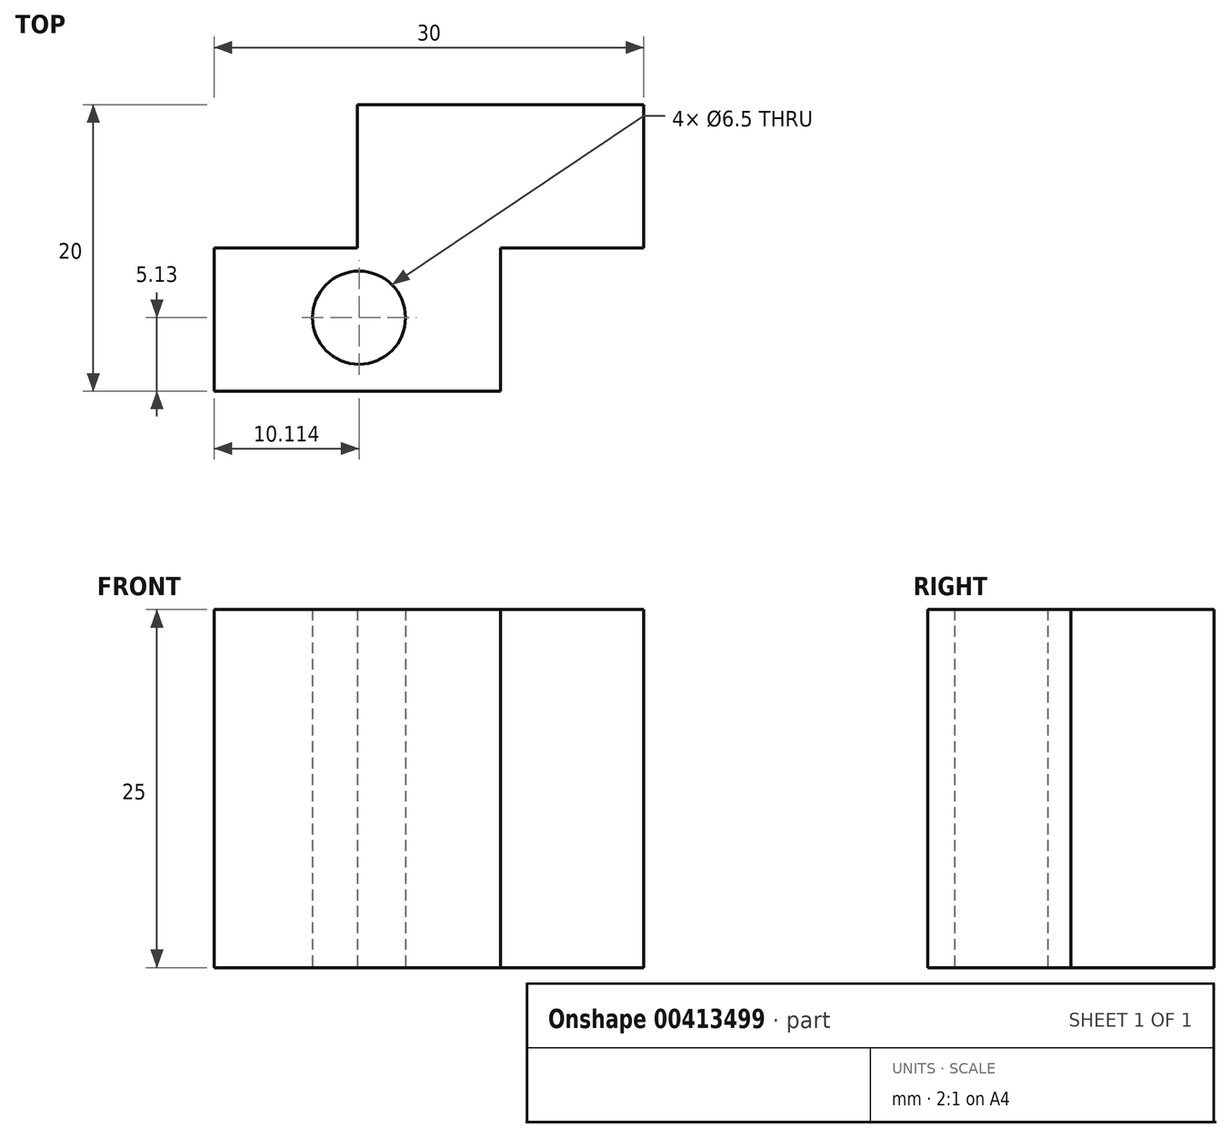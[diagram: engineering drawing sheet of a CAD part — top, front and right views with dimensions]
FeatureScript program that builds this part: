
annotation { "Feature Type Name" : "Feature", "Feature Type Description" : "" }
export const myFeature = defineFeature(function(context is Context, id is Id, definition is map)
    precondition{}
    {
        {
            var Q0;
            Q0=qCreatedBy(makeId("Top.planeOp"),FACE);
            var sketch = newSketch(context, id + "F0", { "sketchPlane" : qUnion([Q0])});
            skLineSegment(sketch, "E0.bottom", {"start": v(-7.6, 20) * mm, "end": v(12.4, 20) * mm});
            skLineSegment(sketch, "E0.top", {"start": v(-7.6, 10) * mm, "end": v(12.4, 10) * mm});
            skLineSegment(sketch, "E0.left", {"start": v(-7.6, 20) * mm, "end": v(-7.6, 10) * mm});
            skLineSegment(sketch, "E0.right", {"start": v(12.4, 20) * mm, "end": v(12.4, 10) * mm});
            skLineSegment(sketch, "E1.bottom", {"start": v(2.4, 10) * mm, "end": v(-17.6, 10) * mm});
            skLineSegment(sketch, "E1.top", {"start": v(2.4, 0) * mm, "end": v(-17.6, 0) * mm});
            skLineSegment(sketch, "E1.left", {"start": v(2.4, 10) * mm, "end": v(2.4, 0) * mm});
            skLineSegment(sketch, "E1.right", {"start": v(-17.6, 10) * mm, "end": v(-17.6, 0) * mm});
            skLineSegment(sketch, "E2.bottom", {"start": v(2.4, 10) * mm, "end": v(22.4, 10) * mm});
            skLineSegment(sketch, "E2.top", {"start": v(2.4, 0) * mm, "end": v(22.4, 0) * mm});
            skLineSegment(sketch, "E2.right", {"start": v(22.4, 10) * mm, "end": v(22.4, 0) * mm});
            skCircle(sketch, "E3", {"center": v(-7.49, 5.13) * mm, "radius": 3.25 * mm});
            skCircle(sketch, "E4", {"center": v(12.34, 4.85) * mm, "radius": 3.25 * mm});
            skPoint(sketch, "E5.end.orphan", {"position": v(12.4, 4.85) * mm});
            skSolve(sketch);
        }
        {
            var Q0;
            Q0=makeQuery(id+"F0.imprint","IMPRINT",FACE,{"disambiguationData":[TD([[makeQuery(id+"F0.imprint","IMPRINT",EDGE,{"derivedFrom":sQuery(id+"F0.wireOp",EDGE,"E0.bottom")}),-1.0]])]});
            var Q1;
            {var subQ4=sQuery(id+"F0.wireOp",EDGE,"E1.left");Q1=makeQuery(id+"F0.imprint","IMPRINT",FACE,{"disambiguationData":[TD([[makeQuery(id+"F0.imprint","IMPRINT",EDGE,{"derivedFrom":subQ4}),1.0]])]});}
            var Q2;
            {var subQ0=sQuery(id+"F0.wireOp",EDGE,"E1.right");Q2=makeQuery(id+"F0.imprint","IMPRINT",FACE,{"disambiguationData":[TD([[makeQuery(id+"F0.imprint","IMPRINT",EDGE,{"derivedFrom":subQ0}),1.0]])]});}
            extrude(context, id + "F1", {"entities" : qUnion([Q0, Q1, Q2]), "depth" : 25 * mm});
        }
    });
